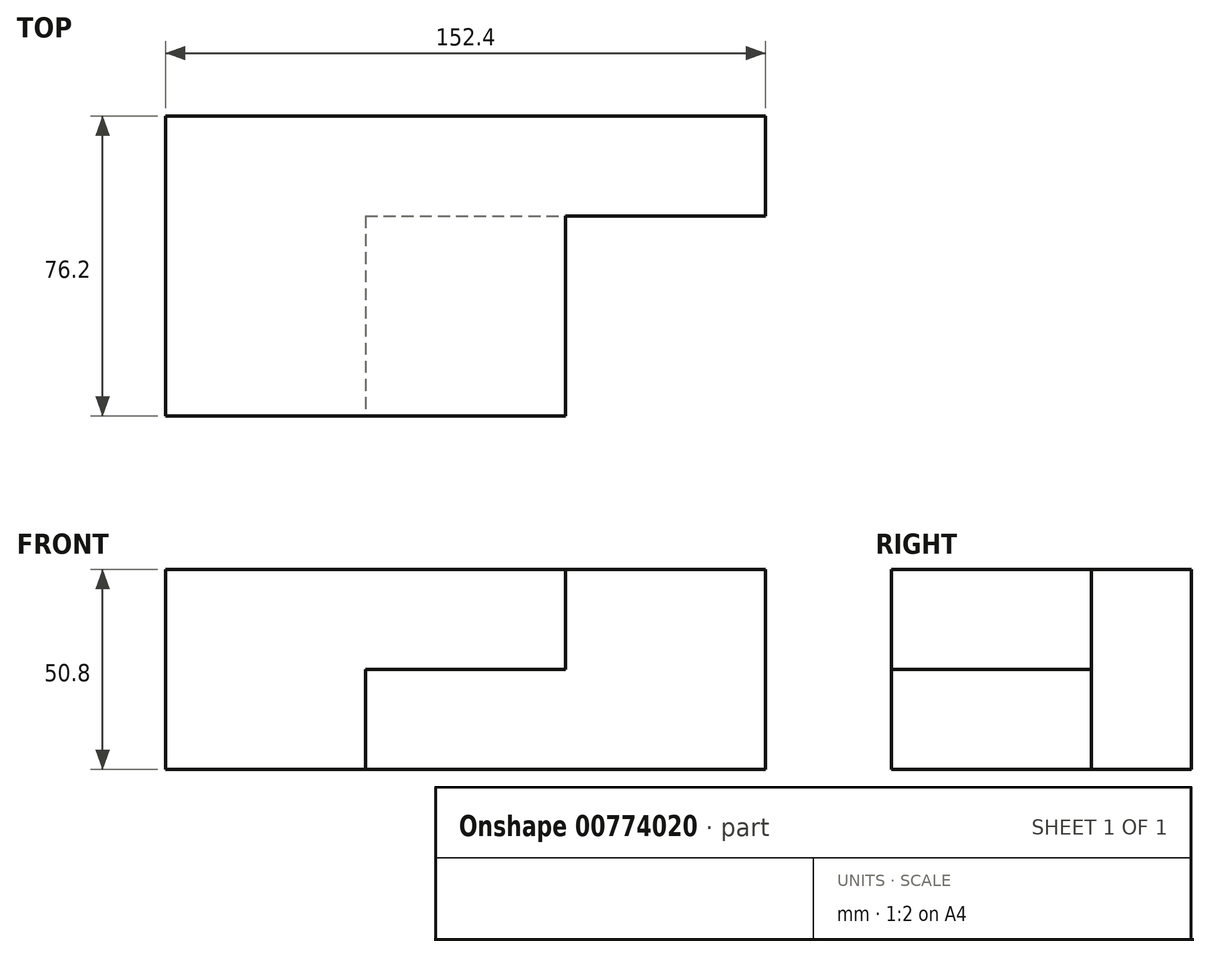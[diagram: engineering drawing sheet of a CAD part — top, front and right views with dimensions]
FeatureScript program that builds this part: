
annotation { "Feature Type Name" : "Feature", "Feature Type Description" : "" }
export const myFeature = defineFeature(function(context is Context, id is Id, definition is map)
    precondition{}
    {
        {
            var Q0;
            Q0=qCreatedBy(makeId("Front.planeOp"),FACE);
            var sketch = newSketch(context, id + "F0", { "sketchPlane" : qUnion([Q0])});
            skLineSegment(sketch, "E0", {"start": v(0, 0) * mm, "end": v(152.4, 0) * mm});
            skLineSegment(sketch, "E1", {"start": v(152.4, 0) * mm, "end": v(152.4, 50.8) * mm});
            skLineSegment(sketch, "E2", {"start": v(152.4, 50.8) * mm, "end": v(0, 50.8) * mm});
            skLineSegment(sketch, "E3", {"start": v(0, 50.8) * mm, "end": v(0, 0) * mm});
            skSolve(sketch);
        }
        {
            var Q0;
            Q0=makeQuery(id+"F0.imprint","IMPRINT",FACE,{"disambiguationData":[TD([[makeQuery(id+"F0.imprint","IMPRINT",EDGE,{"derivedFrom":sQuery(id+"F0.wireOp",EDGE,"E0")}),1.0]])]});
            extrude(context, id + "F1", {"entities" : qUnion([Q0]), "depth" : 76.2 * mm, "offsetDistance" : 25.4 * mm});
        }
        {
            var Q0;
            Q0=makeQuery(id+"F1.opExtrude","CAP_FACE",FACE,{"disambiguationData":[OSD([sQuery(id+"F0.wireOp",EDGE,"E0"),sQuery(id+"F0.wireOp",EDGE,"E1"),sQuery(id+"F0.wireOp",EDGE,"E2"),sQuery(id+"F0.wireOp",EDGE,"E3")])],"isStart":false});
            var sketch = newSketch(context, id + "F2", { "sketchPlane" : qUnion([Q0])});
            skLineSegment(sketch, "E4", {"start": v(50.8, 0) * mm, "end": v(50.8, 25.4) * mm});
            skLineSegment(sketch, "E5", {"start": v(50.8, 25.4) * mm, "end": v(152.4, 25.4) * mm});
            skLineSegment(sketch, "E6", {"start": v(152.4, 25.4) * mm, "end": v(152.4, 0) * mm});
            skLineSegment(sketch, "E7", {"start": v(152.4, 0) * mm, "end": v(50.8, 0) * mm});
            skSolve(sketch);
        }
        {
            var Q0;
            Q0=makeQuery(id+"F2.imprint","IMPRINT",FACE,{"disambiguationData":[TD([[makeQuery(id+"F2.imprint","IMPRINT",EDGE,{"derivedFrom":sQuery(id+"F2.wireOp",EDGE,"E4")}),-1.0]])]});
            extrude(context, id + "F3", {"entities" : qUnion([Q0]), "operationType" : NewBodyOperationType.REMOVE, "oppositeDirection" : true, "depth" : 50.8 * mm, "offsetDistance" : 25.4 * mm});
        }
        {
            var Q0;
            Q0=makeQuery(id+"F1.opExtrude","CAP_FACE",FACE,{"disambiguationData":[OSD([sQuery(id+"F0.wireOp",EDGE,"E0"),sQuery(id+"F0.wireOp",EDGE,"E1"),sQuery(id+"F0.wireOp",EDGE,"E2"),sQuery(id+"F0.wireOp",EDGE,"E3")])],"isStart":false});
            var sketch = newSketch(context, id + "F4", { "sketchPlane" : qUnion([Q0])});
            skLineSegment(sketch, "E8", {"start": v(152.4, 50.8) * mm, "end": v(101.6, 50.8) * mm});
            skLineSegment(sketch, "E9", {"start": v(101.6, 50.8) * mm, "end": v(101.6, 25.4) * mm});
            skLineSegment(sketch, "E10", {"start": v(101.6, 25.4) * mm, "end": v(152.4, 25.4) * mm});
            skLineSegment(sketch, "E11", {"start": v(152.4, 25.4) * mm, "end": v(152.4, 50.8) * mm});
            skSolve(sketch);
        }
        {
            var Q0;
            Q0=makeQuery(id+"F4.imprint","IMPRINT",FACE,{"disambiguationData":[TD([[makeQuery(id+"F4.imprint","IMPRINT",EDGE,{"derivedFrom":sQuery(id+"F4.wireOp",EDGE,"E8")}),1.0]])]});
            extrude(context, id + "F5", {"entities" : qUnion([Q0]), "operationType" : NewBodyOperationType.REMOVE, "oppositeDirection" : true, "depth" : 50.8 * mm, "offsetDistance" : 25.4 * mm});
        }
    });
